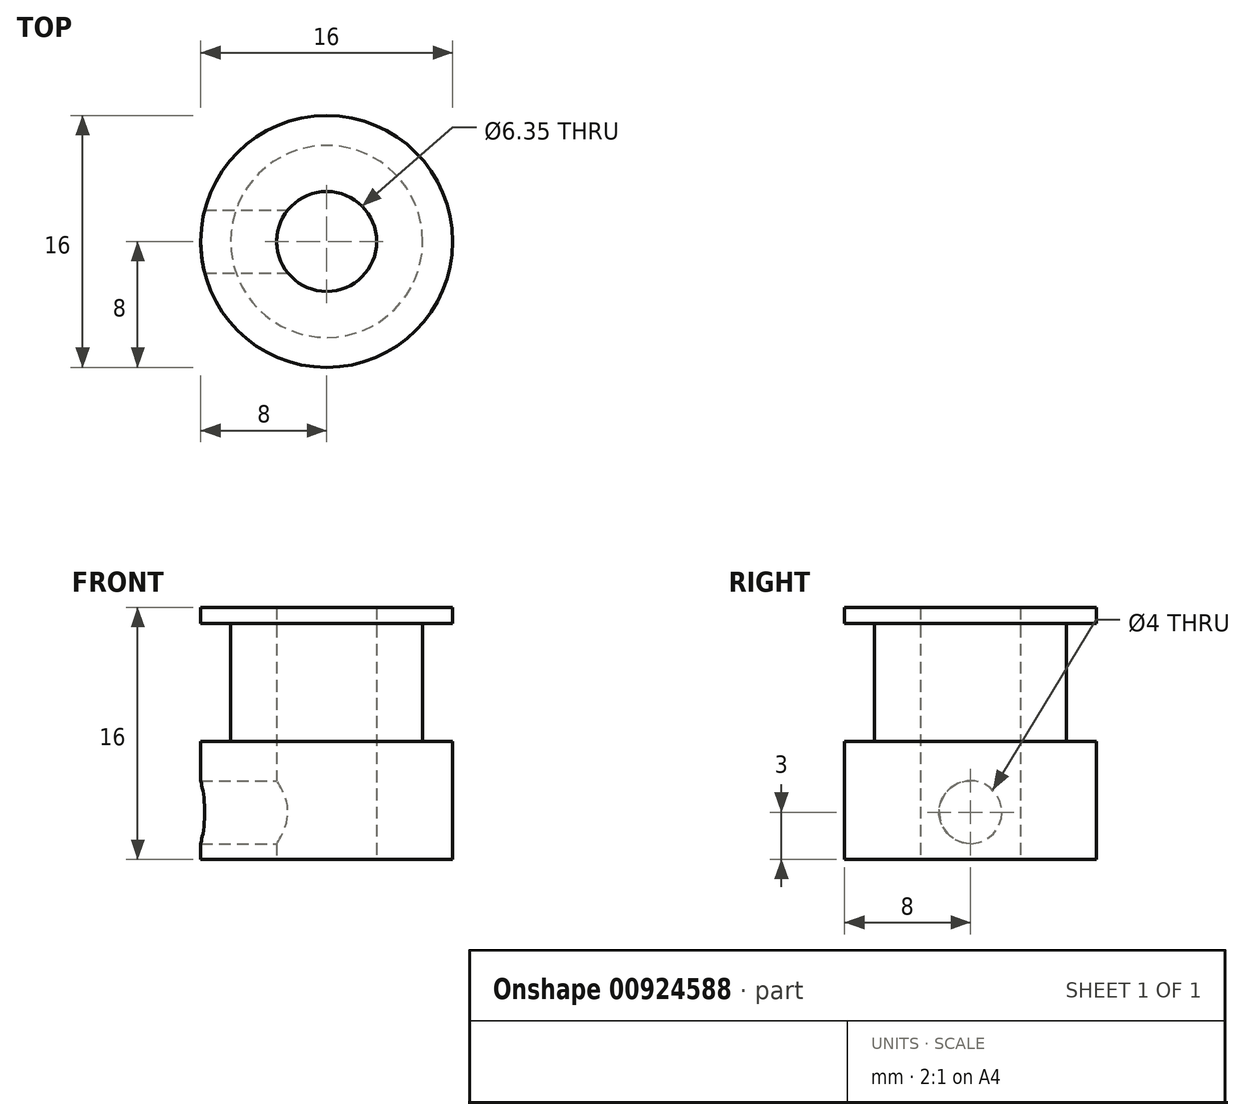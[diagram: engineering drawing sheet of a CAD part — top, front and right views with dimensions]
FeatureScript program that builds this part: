
annotation { "Feature Type Name" : "Feature", "Feature Type Description" : "" }
export const myFeature = defineFeature(function(context is Context, id is Id, definition is map)
    precondition{}
    {
        {
            var Q0;
            Q0=qCreatedBy(makeId("Front.planeOp"),FACE);
            var sketch = newSketch(context, id + "F0", { "sketchPlane" : qUnion([Q0])});
            skLineSegment(sketch, "E0", {"start": v(0, 40.72) * mm, "end": v(0, -42.36) * mm, "construction": true});
            skLineSegment(sketch, "E1", {"start": v(0, -8) * mm, "end": v(-8, -8) * mm});
            skLineSegment(sketch, "E2", {"start": v(-8, -8) * mm, "end": v(-8, -0.5) * mm});
            skLineSegment(sketch, "E3", {"start": v(-8, 8) * mm, "end": v(0, 8) * mm});
            skLineSegment(sketch, "E4", {"start": v(0, 8) * mm, "end": v(0, -8) * mm});
            skLineSegment(sketch, "E5", {"start": v(-8, 7) * mm, "end": v(-6.1, 7) * mm});
            skLineSegment(sketch, "E6", {"start": v(-6.1, 7) * mm, "end": v(-6.1, -0.5) * mm});
            skLineSegment(sketch, "E7", {"start": v(-6.1, -0.5) * mm, "end": v(-8, -0.5) * mm});
            skLineSegment(sketch, "E8.trimOffspring", {"start": v(-8, 7) * mm, "end": v(-8, 8) * mm});
            skSolve(sketch);
        }
        {
            var Q0;
            Q0=makeQuery(id+"F0.imprint","IMPRINT",FACE,{"disambiguationData":[TD([[makeQuery(id+"F0.imprint","IMPRINT",EDGE,{"derivedFrom":sQuery(id+"F0.wireOp",EDGE,"E1")}),-1.0]])]});
            var Q1;
            Q1=sQuery(id+"F0.wireOp",EDGE,"E0");
            revolve(context, id + "F1", {"surfaceOperationType" : NewSurfaceOperationType.NEW, "entities" : qUnion([Q0]), "axis" : qUnion([Q1]), "revolveType" : RevolveType.FULL});
        }
        {
            var Q0;
            Q0=makeQuery(id+"F1.opRevolve","SWEPT_FACE",FACE,{"disambiguationData":[OSD([sQuery(id+"F0.wireOp",EDGE,"E1")])]});
            var sketch = newSketch(context, id + "F2", { "sketchPlane" : qUnion([Q0])});
            skCircle(sketch, "E9", {"center": v(0, 0) * mm, "radius": 3.17 * mm});
            skSolve(sketch);
        }
        {
            var Q0;
            Q0=makeQuery(id+"F2.imprint","IMPRINT",FACE,{"disambiguationData":[TD([[makeQuery(id+"F2.imprint","IMPRINT",EDGE,{"derivedFrom":sQuery(id+"F2.wireOp",EDGE,"E9")}),1.0]])]});
            extrude(context, id + "F3", {"entities" : qUnion([Q0]), "operationType" : NewBodyOperationType.REMOVE, "oppositeDirection" : true, "depth" : 25 * mm, "offsetDistance" : 25 * mm});
        }
        {
            var Q0;
            Q0=qCreatedBy(makeId("Right.planeOp"),FACE);
            var sketch = newSketch(context, id + "F4", { "sketchPlane" : qUnion([Q0])});
            skCircle(sketch, "E10", {"center": v(0, -5) * mm, "radius": 2 * mm});
            skSolve(sketch);
        }
        {
            var Q0;
            Q0=makeQuery(id+"F4.imprint","IMPRINT",FACE,{"disambiguationData":[TD([[makeQuery(id+"F4.imprint","IMPRINT",EDGE,{"derivedFrom":sQuery(id+"F4.wireOp",EDGE,"E10")}),1.0]])]});
            extrude(context, id + "F5", {"entities" : qUnion([Q0]), "operationType" : NewBodyOperationType.REMOVE, "oppositeDirection" : true, "depth" : 25 * mm, "offsetDistance" : 25 * mm});
        }
    });
